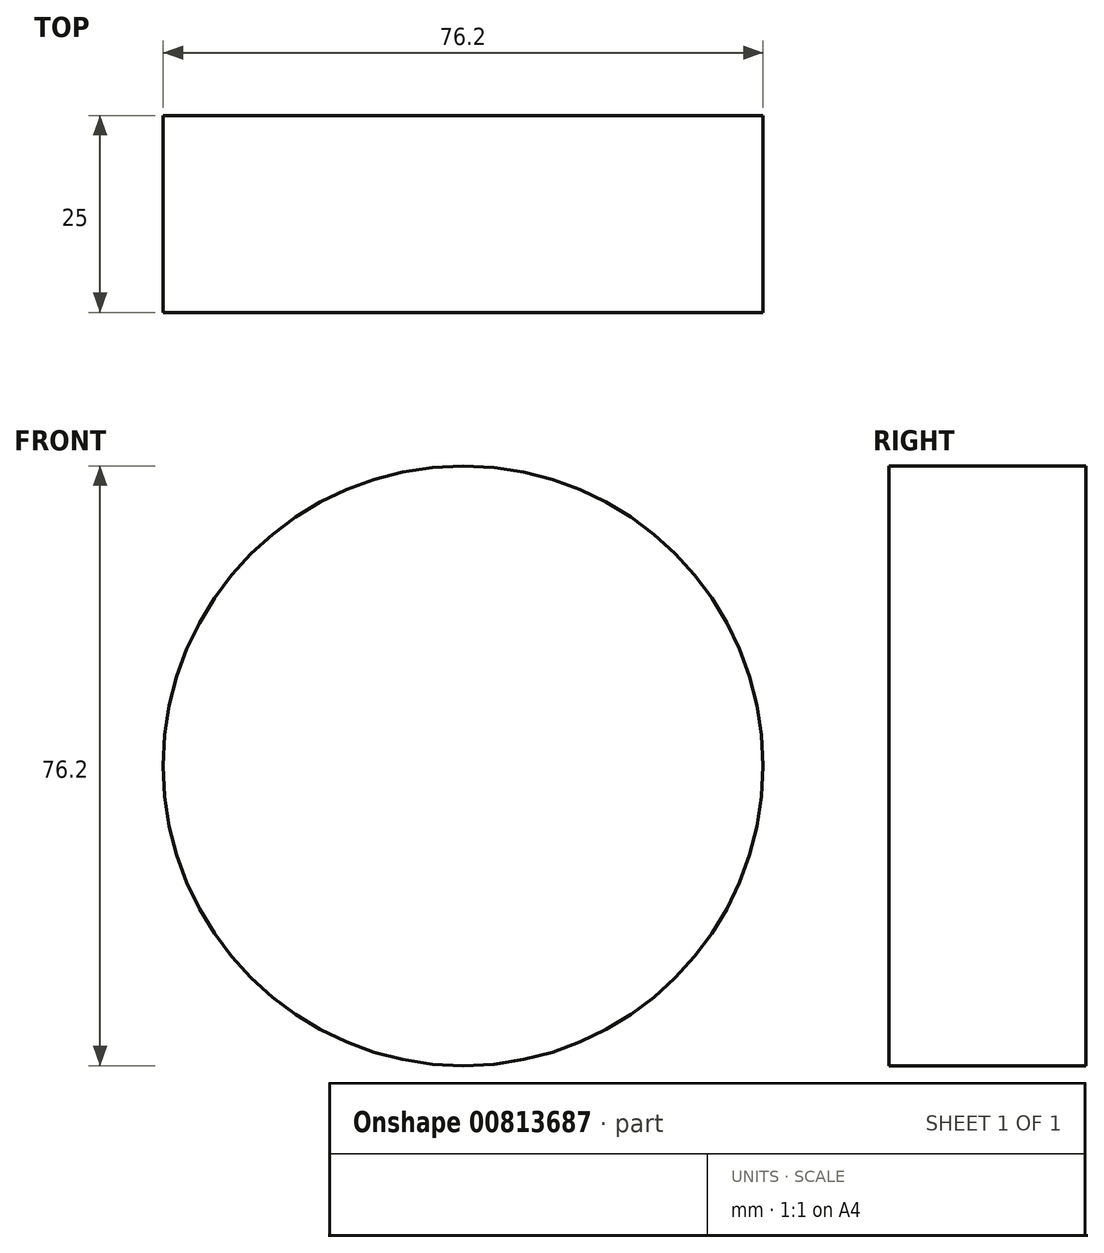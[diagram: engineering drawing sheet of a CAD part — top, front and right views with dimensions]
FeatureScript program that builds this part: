
annotation { "Feature Type Name" : "Feature", "Feature Type Description" : "" }
export const myFeature = defineFeature(function(context is Context, id is Id, definition is map)
    precondition{}
    {
        {
            var Q0;
            Q0=qCreatedBy(makeId("Front.planeOp"),FACE);
            var sketch = newSketch(context, id + "F0", { "sketchPlane" : qUnion([Q0])});
            skCircle(sketch, "E0", {"center": v(0, 0) * mm, "radius": 38.1 * mm});
            skSolve(sketch);
        }
        {
            var Q0;
            Q0 = qSketchRegion(id + "F0", true);
            extrude(context, id + "F1", {"entities" : qUnion([Q0]), "depth" : 25 * mm, "offsetDistance" : 25 * mm});
        }
    });
